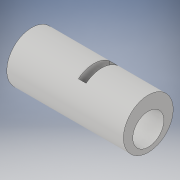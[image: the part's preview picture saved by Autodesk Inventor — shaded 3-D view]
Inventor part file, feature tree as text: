
AUTODESK INVENTOR PART (.ipt)
format: ipt  version: 2019 (Build 230136000, 136)  size: 256,512 bytes
history: native  units: in
note: dims shown in document units (in); Inventor stores cm internally (conversion verified against a paired STEP export)
features: sketch x9, extrude x4, revolve x1, loft x1, fillet x1, plane x1, other x1
ambient origin geometry x8: Origin, YZ Plane, XZ Plane, XY Plane, X Axis, Y Axis, Z Axis, Center Point
bodies: Solid1 (feature_tree)
feature tree (18):
  revolve  "Revolution1"  [1 undecoded]
  sketch  "Sketch2"  dims[d3=0.7874in d4=90.0deg]
  extrude  "Extrusion1"  TaperAngle=90.0deg  [1 undecoded]
  sketch  "Sketch4"  dims[d9=0.7874in d10=0.0in d11=90.0deg]
  sketch  "Sketch5"  dims[d12=0.0in d13=90.0deg d14=0.2362in]
  loft  "Loft1"
  fillet  "Fillet1"  Radius=0.3937in
  sketch  "Sketch6"  dims[d15=0.5118in d16=0.1969in d17=0.0in]
  plane  "Work Plane1"
  extrude  "Extrusion2"  TaperAngle=0.0deg  [1 undecoded]
  extrude  "Extrusion3"  Depth=0.2362in
  extrude  "Extrusion4"  Depth=0.1969in TaperAngle=0.0deg
  sketch  "Sketch1"  dims[d0=0.1181in d1=0.7874in]
  sketch  "Sketch3"  dims[d5=0.0591in d6=0.5118in d7=0.3937in d8=0.0in]
  other  "Edges1"
  sketch  "Sketch7"  dims[d18=0.6299in]
  sketch  "Sketch8"  dims[d19=0.7177in]
  sketch  "Sketch9"  dims[d22=0.3937in d24=0.1969in d25=0.0in d26=1.2598in d28=0.3937in d29=0.1199in d30=1.1811in d31=0.0in]
note: 3 required parameter values undecoded (feature->parameter linkage not recoverable at this tier; creation-order binding heuristic only, values carry confidence <= 0.55)